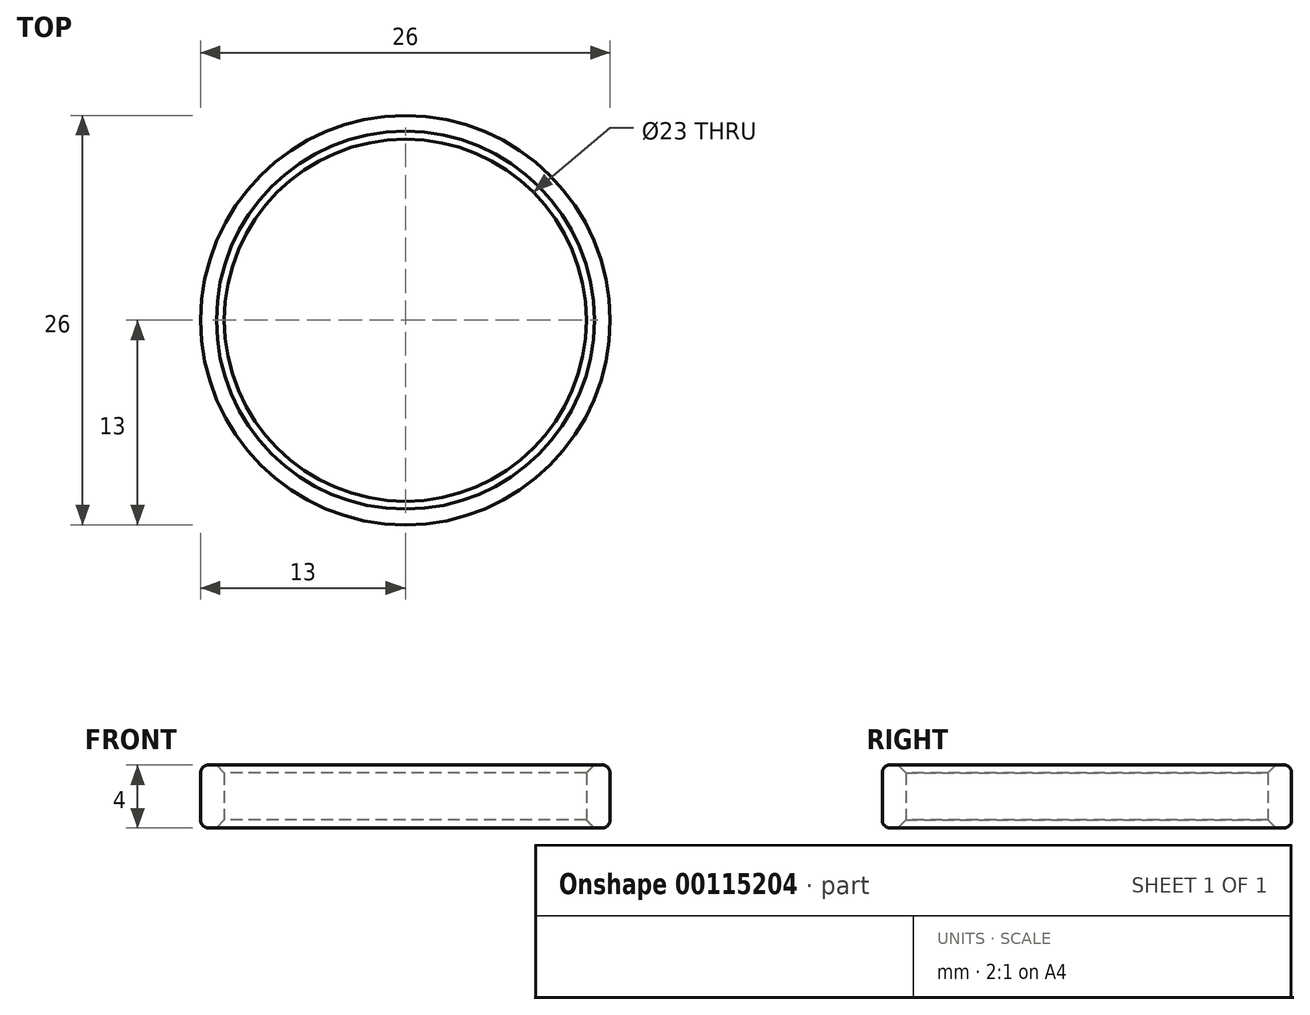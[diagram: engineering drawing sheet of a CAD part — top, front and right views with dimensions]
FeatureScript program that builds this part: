
annotation { "Feature Type Name" : "Feature", "Feature Type Description" : "" }
export const myFeature = defineFeature(function(context is Context, id is Id, definition is map)
    precondition{}
    {
        {
            var Q0;
            Q0=qCreatedBy(makeId("Top.planeOp"),FACE);
            var sketch = newSketch(context, id + "F0", { "sketchPlane" : qUnion([Q0])});
            skCircle(sketch, "E0", {"center": v(0, 0) * mm, "radius": 13 * mm});
            skCircle(sketch, "E1", {"center": v(0, 0) * mm, "radius": 11.5 * mm});
            skSolve(sketch);
        }
        {
            var Q0;
            Q0=makeQuery(id+"F0.imprint","IMPRINT",FACE,{"disambiguationData":[TD([[makeQuery(id+"F0.imprint","IMPRINT",EDGE,{"derivedFrom":sQuery(id+"F0.wireOp",EDGE,"E0")}),1.0]])]});
            extrude(context, id + "F1", {"entities" : qUnion([Q0]), "depth" : 4 * mm});
        }
        {
            var Q0;
            Q0=makeQuery(id+"F1.opExtrude","CAP_EDGE",EDGE,{"disambiguationData":[OSD([sQuery(id+"F0.wireOp",EDGE,"E1")])],"isStart":false});
            var Q1;
            Q1=makeQuery(id+"F1.opExtrude","CAP_EDGE",EDGE,{"disambiguationData":[OSD([sQuery(id+"F0.wireOp",EDGE,"E1")])],"isStart":true});
            chamfer(context, id + "F2", {"entities" : qUnion([Q0, Q1]), "width" : 0.5 * mm, "tangentPropagation" : true});
        }
        {
            var Q0;
            Q0=makeQuery(id+"F1.opExtrude","CAP_EDGE",EDGE,{"disambiguationData":[OSD([sQuery(id+"F0.wireOp",EDGE,"E0")])],"isStart":false});
            var Q1;
            Q1=makeQuery(id+"F1.opExtrude","CAP_EDGE",EDGE,{"disambiguationData":[OSD([sQuery(id+"F0.wireOp",EDGE,"E0")])],"isStart":true});
            fillet(context, id + "F3", {"entities" : qUnion([Q0, Q1]), "radius" : 0.5 * mm, "tangentPropagation" : true, "allowEdgeOverflow" : false});
        }
    });
